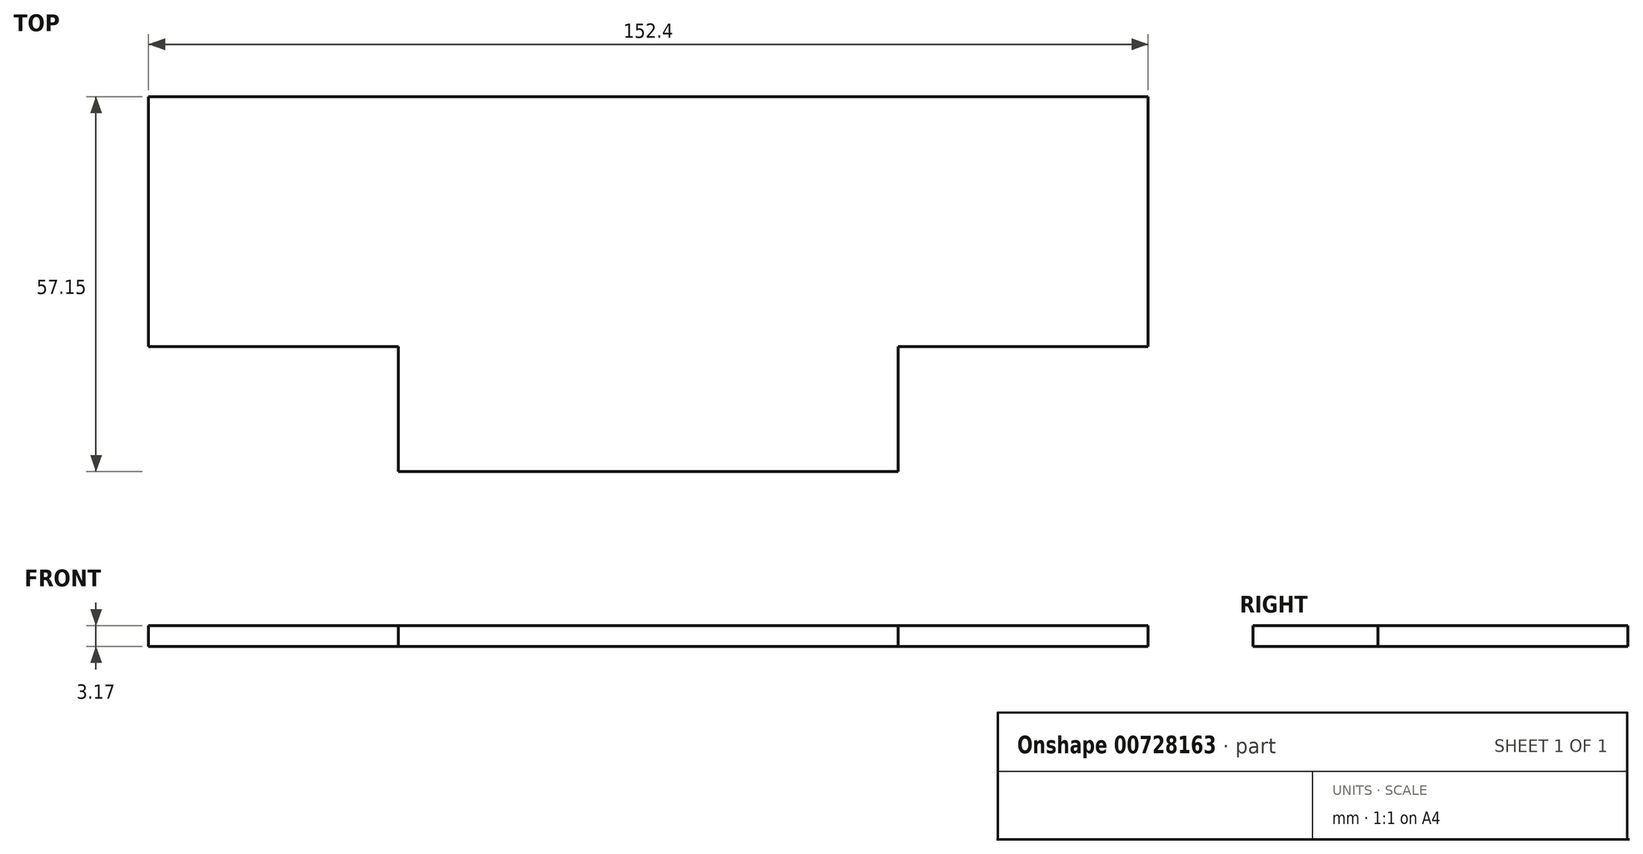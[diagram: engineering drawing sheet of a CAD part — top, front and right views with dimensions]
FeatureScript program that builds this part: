
annotation { "Feature Type Name" : "Feature", "Feature Type Description" : "" }
export const myFeature = defineFeature(function(context is Context, id is Id, definition is map)
    precondition{}
    {
        {
            var Q0;
            Q0=qCreatedBy(makeId("Top.planeOp"),FACE);
            var sketch = newSketch(context, id + "F0", { "sketchPlane" : qUnion([Q0])});
            skLineSegment(sketch, "E0", {"start": v(-133.18, 28.35) * mm, "end": v(-133.18, -22.45) * mm});
            skLineSegment(sketch, "E1", {"start": v(19.22, -22.45) * mm, "end": v(19.22, 28.35) * mm});
            skLineSegment(sketch, "E2", {"start": v(19.22, 28.35) * mm, "end": v(-133.18, 28.35) * mm});
            skLineSegment(sketch, "E3.MirrorCS", {"start": v(19.22, -9.75) * mm, "end": v(-18.88, -9.75) * mm});
            skLineSegment(sketch, "E4", {"start": v(-18.88, -9.75) * mm, "end": v(-18.88, -22.45) * mm});
            skLineSegment(sketch, "E5.MirrorCS", {"start": v(-133.18, -9.75) * mm, "end": v(-95.08, -9.75) * mm});
            skLineSegment(sketch, "E6", {"start": v(-18.88, -9.75) * mm, "end": v(-18.88, -28.8) * mm});
            skLineSegment(sketch, "E7", {"start": v(-95.08, -9.75) * mm, "end": v(-95.08, -28.8) * mm});
            skLineSegment(sketch, "E8", {"start": v(-95.08, -28.8) * mm, "end": v(-18.88, -28.8) * mm});
            skSolve(sketch);
        }
        {
            var Q0;
            {var subQ0=sQuery(id+"F0.wireOp",EDGE,"E2");Q0=makeQuery(id+"F0.imprint","IMPRINT",FACE,{"disambiguationData":[TD([[makeQuery(id+"F0.imprint","IMPRINT",EDGE,{"derivedFrom":subQ0}),1.0]])]});}
            extrude(context, id + "F1", {"entities" : qUnion([Q0]), "depth" : 3.17 * mm, "offsetDistance" : 25.4 * mm});
        }
    });
